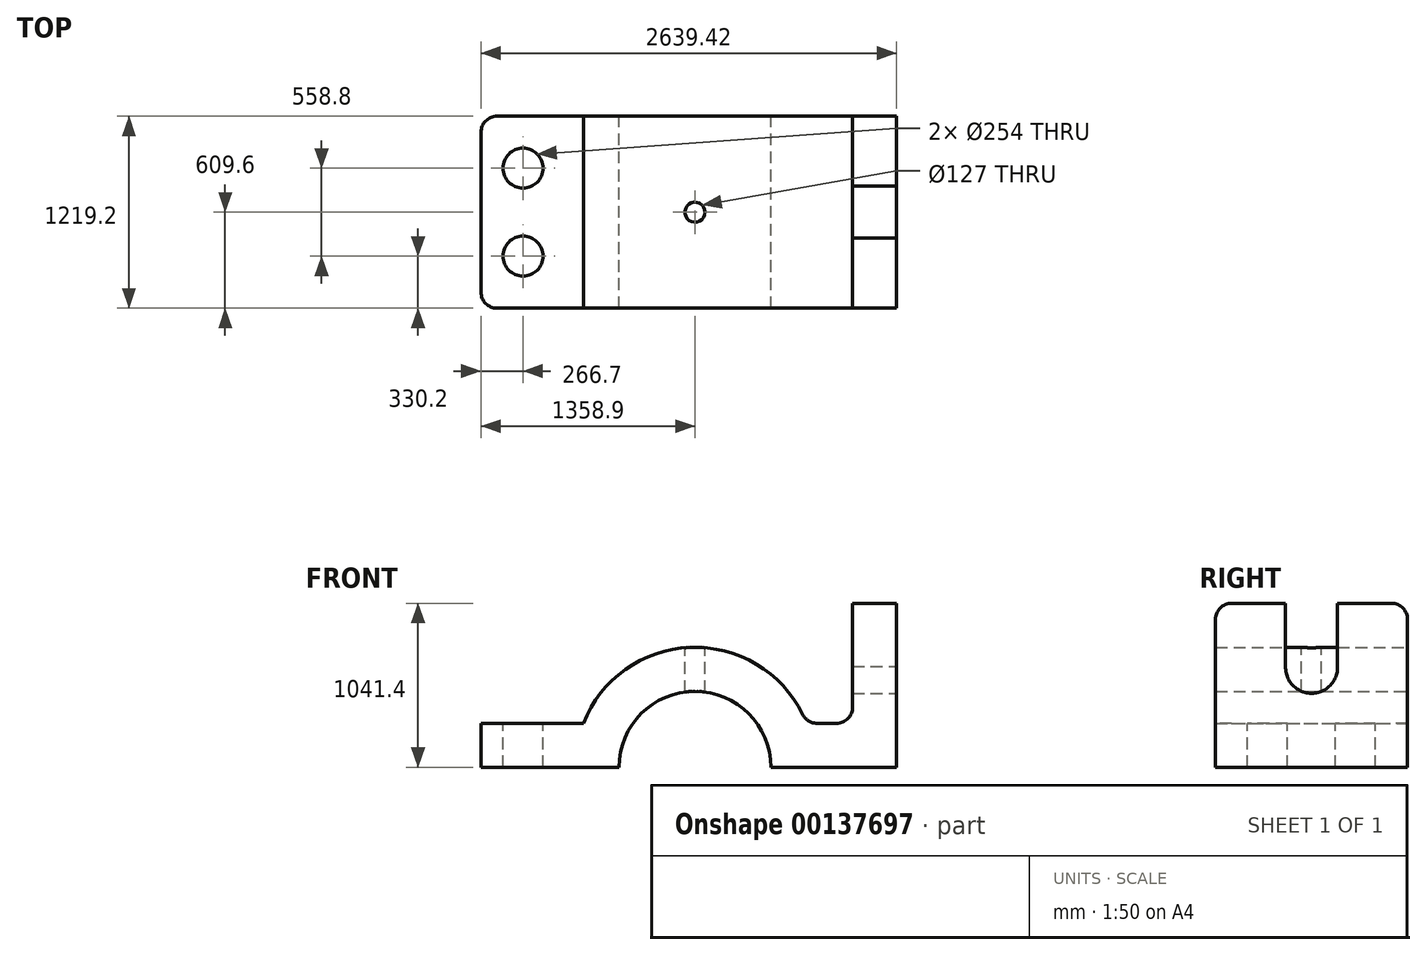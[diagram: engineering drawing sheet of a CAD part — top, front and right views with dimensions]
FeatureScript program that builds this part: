
annotation { "Feature Type Name" : "Feature", "Feature Type Description" : "" }
export const myFeature = defineFeature(function(context is Context, id is Id, definition is map)
    precondition{}
    {
        {
            var Q0;
            Q0=qCreatedBy(makeId("Front.planeOp"),FACE);
            var sketch = newSketch(context, id + "F0", { "sketchPlane" : qUnion([Q0])});
            skArc(sketch, "E0", {"start": v(482.22, 0) * mm, "mid": v(0, 482.22) * mm, "end": v(-482.22, 0) * mm});
            skArc(sketch, "E1", {"start": v(708.93, 279.4) * mm, "mid": v(0, 762) * mm, "end": v(-708.93, 279.4) * mm});
            skLineSegment(sketch, "E2", {"start": v(-482.22, 0) * mm, "end": v(-1358.9, 0) * mm});
            skLineSegment(sketch, "E3", {"start": v(-1358.9, 0) * mm, "end": v(-1358.9, 279.4) * mm});
            skLineSegment(sketch, "E4", {"start": v(-1358.9, 279.4) * mm, "end": v(-708.93, 279.4) * mm});
            skLineSegment(sketch, "E5", {"start": v(482.22, 0) * mm, "end": v(1280.52, 0) * mm});
            skLineSegment(sketch, "E6", {"start": v(1280.52, 0) * mm, "end": v(1280.52, 279.4) * mm});
            skLineSegment(sketch, "E7.trimOffspring", {"start": v(708.93, 279.4) * mm, "end": v(1001.12, 279.4) * mm});
            skLineSegment(sketch, "E8", {"start": v(1280.52, 0) * mm, "end": v(1280.52, 1041.4) * mm});
            skLineSegment(sketch, "E9", {"start": v(1280.52, 1041.4) * mm, "end": v(1001.12, 1041.4) * mm});
            skLineSegment(sketch, "E10", {"start": v(1001.12, 1041.4) * mm, "end": v(1001.12, 279.4) * mm});
            skPoint(sketch, "E10.endSnap0", {"position": v(994.72, 279.4) * mm});
            skSolve(sketch);
        }
        {
            var Q0;
            Q0 = qSketchRegion(id + "F0", true);
            extrude(context, id + "F1", {"entities" : qUnion([Q0]), "depth" : 1219.2 * mm});
        }
        {
            var Q0;
            Q0=makeQuery(id+"F1.opExtrude","SWEPT_FACE",FACE,{"disambiguationData":[OSD([sQuery(id+"F0.wireOp",EDGE,"E8")])]});
            var sketch = newSketch(context, id + "F2", { "sketchPlane" : qUnion([Q0])});
            skArc(sketch, "E11", {"start": v(-774.59, 641.06) * mm, "mid": v(-610.11, 469.9) * mm, "end": v(-444.58, 640.04) * mm});
            skPoint(sketch, "E11.centerSnap0", {"position": v(-609.6, 0) * mm});
            skLineSegment(sketch, "E12", {"start": v(-444.58, 640.04) * mm, "end": v(-444.58, 1041.4) * mm});
            skLineSegment(sketch, "E13", {"start": v(-774.59, 641.06) * mm, "end": v(-774.59, 1041.4) * mm});
            skLineSegment(sketch, "E14", {"start": v(-774.59, 1041.4) * mm, "end": v(-444.58, 1041.4) * mm});
            skSolve(sketch);
        }
        {
            var Q0;
            Q0 = qSketchRegion(id + "F2", true);
            extrude(context, id + "F3", {"entities" : qUnion([Q0]), "operationType" : NewBodyOperationType.REMOVE, "oppositeDirection" : true, "depth" : 526.83 * mm});
        }
        {
            var Q0;
            Q0=makeQuery(id+"F1.opExtrude","SWEPT_FACE",FACE,{"disambiguationData":[OSD([sQuery(id+"F0.wireOp",EDGE,"E4")])]});
            var sketch = newSketch(context, id + "F4", { "sketchPlane" : qUnion([Q0])});
            skCircle(sketch, "E15", {"center": v(-1092.2, -889) * mm, "radius": 127 * mm});
            skCircle(sketch, "E16", {"center": v(-1092.2, -330.2) * mm, "radius": 127 * mm});
            skCircle(sketch, "E17", {"center": v(0, -609.6) * mm, "radius": 63.5 * mm});
            skSolve(sketch);
        }
        {
            var Q0;
            Q0 = qSketchRegion(id + "F4", true);
            extrude(context, id + "F5", {"entities" : qUnion([Q0]), "operationType" : NewBodyOperationType.REMOVE, "endBound" : BoundingType.THROUGH_ALL, "oppositeDirection" : true, "depth" : 25.4 * mm, "hasSecondDirection" : true, "secondDirectionBound" : SecondDirectionBoundingType.THROUGH_ALL, "secondDirectionOppositeDirection" : false, "secondDirectionDepth" : 25.4 * mm});
        }
        {
            var Q0;
            Q0=makeQuery(id+"F1.opExtrude","CAP_EDGE",EDGE,{"disambiguationData":[OSD([sQuery(id+"F0.wireOp",EDGE,"E9")])],"isStart":false});
            var Q1;
            Q1=makeQuery(id+"F1.opExtrude","SWEPT_EDGE",EDGE,{"disambiguationData":[OSD([sQuery(id+"F0.wireOp",EDGE,"E7.trimOffspring"),sQuery(id+"F0.wireOp",EDGE,"E10")])]});
            var Q2;
            Q2=makeQuery(id+"F1.opExtrude","CAP_EDGE",EDGE,{"disambiguationData":[OSD([sQuery(id+"F0.wireOp",EDGE,"E3")])],"isStart":false});
            var Q3;
            Q3=makeQuery(id+"F1.opExtrude","CAP_EDGE",EDGE,{"disambiguationData":[OSD([sQuery(id+"F0.wireOp",EDGE,"E9")])],"isStart":true});
            var Q4;
            Q4=makeQuery(id+"F1.opExtrude","CAP_EDGE",EDGE,{"disambiguationData":[OSD([sQuery(id+"F0.wireOp",EDGE,"E3")])],"isStart":true});
            var Q5;
            Q5=makeQuery(id+"F1.opExtrude","SWEPT_EDGE",EDGE,{"disambiguationData":[OSD([sQuery(id+"F0.wireOp",EDGE,"E1"),sQuery(id+"F0.wireOp",EDGE,"E7.trimOffspring")])]});
            fillet(context, id + "F6", {"entities" : qUnion([Q0, Q1, Q2, Q3, Q4, Q5]), "radius" : 101.6 * mm, "tangentPropagation" : true, "allowEdgeOverflow" : false});
        }
    });
